# Revit family: Varmax_180_225_2-3Piquages - depuis 2013-12_FR_C
name_source: partatom
category: Equipement de génie climatique
revit_build: Autodesk Revit 2015 (Build: 20140606_1530(x64)
units: mm (PartAtom-declared; Revit-internal decimal feet)

## types (2) — shared parameters
Classe Nox = 6
Fabricant = Atlantic
Famille = Chaudière collective sol gaz
Fréquence = 50 Hz
Garantie autres pièces = 2 ans
Garantie corps de chauffe = 3 ans
Hauteur = 1780 mm  [stored 5.8399 ft]
Hauteur chaudière (hors pieds) = 1780 mm  [stored 5.8399 ft]
Hauteur de pieds mini = 45 mm
Hauteur entrée d’air (hors pieds) = 1564 mm
Hauteur piquage départ (hors pieds) = 1606 mm  [stored 5.26903 ft]
Hauteur piquage gaz (hors pieds) = 1315 mm  [stored 4.3143 ft]
Hauteur piquage retour chaud (hors pieds) = 1171 mm  [stored 3.84186 ft]
Largeur = 734 mm  [stored 2.40814 ft]
Largeur chaudière = 701 mm  [stored 2.29987 ft]
Largeur chaudière avec jaquette = 734 mm  [stored 2.40814 ft]
Lien données RT (Edibatec) = http://www.edibatec.org
Lien page produit = http://www.atlantic-guillot.fr
Lien pièces détachées = http://atlantic.plateforme-services.com
Longueur piquages départ / retour = 148 mm
Marque commerciale = Oui
Marque3D = Oui
Matériau corps de chauffe = Acier inoxydable
Modèle = Varmax 180
Nombre piquages = 3
Poids à vide = 393 kg
Pression d'alimentation gaz naturel = 20 ou 300 mbar
Pression d'alimentation propane = 37 mbar
Pression de service = 6 bar
Profondeur = 1218 mm  [stored 3.99606 ft]
Profondeur chaudière = 1218 mm  [stored 3.99606 ft]
Raccordement fumées = Cheminée (B23/B23p) / Ventouse (C13/C33/C53)
Réseau (mono/tri) = Monophasé
Taux de modulation = 0.2
Tension d'alimentation = 230 V
Type d'énergie = Gaz naturel ou Propane
URL = www.atlantic-guillot.fr
température de consigne départ maximale = 85 °C
volume en eau = 151 l
Ø evacuation condensats = 25 mm  [stored 0.082021 ft]
Ø nominal 1er retour froid = 65 mm  [stored 0.213255 ft]
Ø nominal 2eme retour chaud = 65 mm  [stored 0.213255 ft]
Ø nominal départ = 65 mm  [stored 0.213255 ft]
Ø nominal piquage gaz = 49 mm  [stored 0.160761 ft]
Ø nominal vidange condensateur = 25 mm  [stored 0.082021 ft]
Ø nominal vidange échangeur = 25 mm  [stored 0.082021 ft]
Ø piquage soupape = 25 mm  [stored 0.082021 ft]
Ø_Entrée d'air = 150 mm
Ø_Sortie fumées = 150 mm

## per-type parameters (varying)
| type | Code article | Description | Puissance utile nominale à régime 50/30 °C | Puissance utile nominale à régime 80/60 °C | Puissance électrique absorbée à Qn |
| VARMAX 180 20MB 2-3 PIQUAGES | 541508 | Chaudière sol gaz à condensation en inox 180 kW 2/3 piquages | 191 kW | 175 kW | 179 VA |
| VARMAX 225 20MB 2-3 PIQUAGES | 541513 | Chaudière sol gaz à condensation en inox 225 kW 2/3 piquages | 238 kW | 219 kW | 320 VA |

note: column(s) folded — value = type name in every type: Référence

note: [stored X ft] marks values corroborated as IEEE doubles in the binary element streams (Revit-internal decimal feet)

## geometry (parser evidence)
native form markers: Sweep x2
no freeform markers — native parametric forms only
